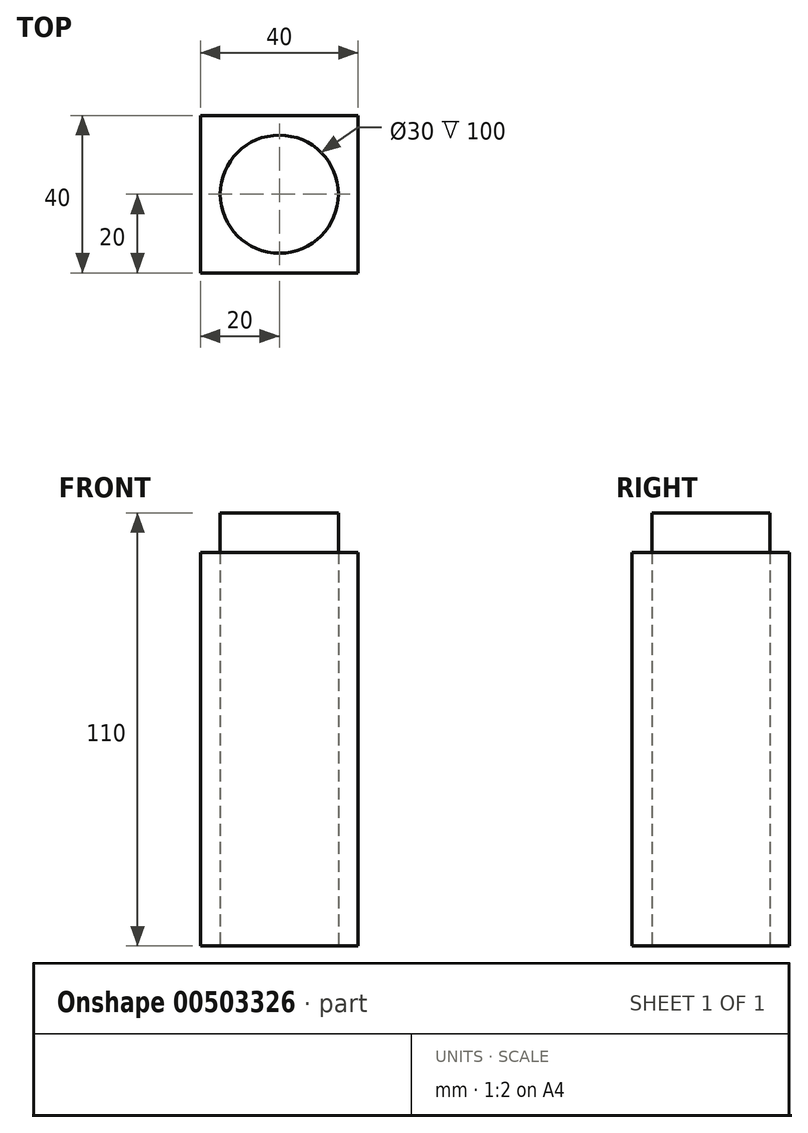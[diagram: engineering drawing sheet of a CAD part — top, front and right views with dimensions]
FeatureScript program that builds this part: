
annotation { "Feature Type Name" : "Feature", "Feature Type Description" : "" }
export const myFeature = defineFeature(function(context is Context, id is Id, definition is map)
    precondition{}
    {
        {
            var Q0;
            Q0=qCreatedBy(makeId("Top.planeOp"),FACE);
            var sketch = newSketch(context, id + "F0", { "sketchPlane" : qUnion([Q0])});
            skLineSegment(sketch, "E0.bottom", {"start": v(20, -20) * mm, "end": v(-20, -20) * mm});
            skLineSegment(sketch, "E0.top", {"start": v(20, 20) * mm, "end": v(-20, 20) * mm});
            skLineSegment(sketch, "E0.left", {"start": v(20, -20) * mm, "end": v(20, 20) * mm});
            skLineSegment(sketch, "E0.right", {"start": v(-20, -20) * mm, "end": v(-20, 20) * mm});
            skPoint(sketch, "E0.middle", {"position": v(0, 0) * mm});
            skCircle(sketch, "E1", {"center": v(0, 0) * mm, "radius": 15 * mm});
            skSolve(sketch);
        }
        {
            var Q0;
            Q0=makeQuery(id+"F0.imprint","IMPRINT",FACE,{"disambiguationData":[TD([[makeQuery(id+"F0.imprint","IMPRINT",EDGE,{"derivedFrom":sQuery(id+"F0.wireOp",EDGE,"E0.bottom")}),-1.0]])]});
            extrude(context, id + "F1", {"entities" : qUnion([Q0]), "depth" : 100 * mm});
        }
        {
            var Q0;
            Q0=qCreatedBy(makeId("Top.planeOp"),FACE);
            var sketch = newSketch(context, id + "F2", { "sketchPlane" : qUnion([Q0])});
            skCircle(sketch, "E2.0", {"center": v(0, 0) * mm, "radius": 15 * mm});
            skSolve(sketch);
        }
        {
            var Q0;
            Q0=qSketchRegion(id+"F2",true);
            extrude(context, id + "F3", {"entities" : qUnion([Q0]), "depth" : 110 * mm});
        }
    });
